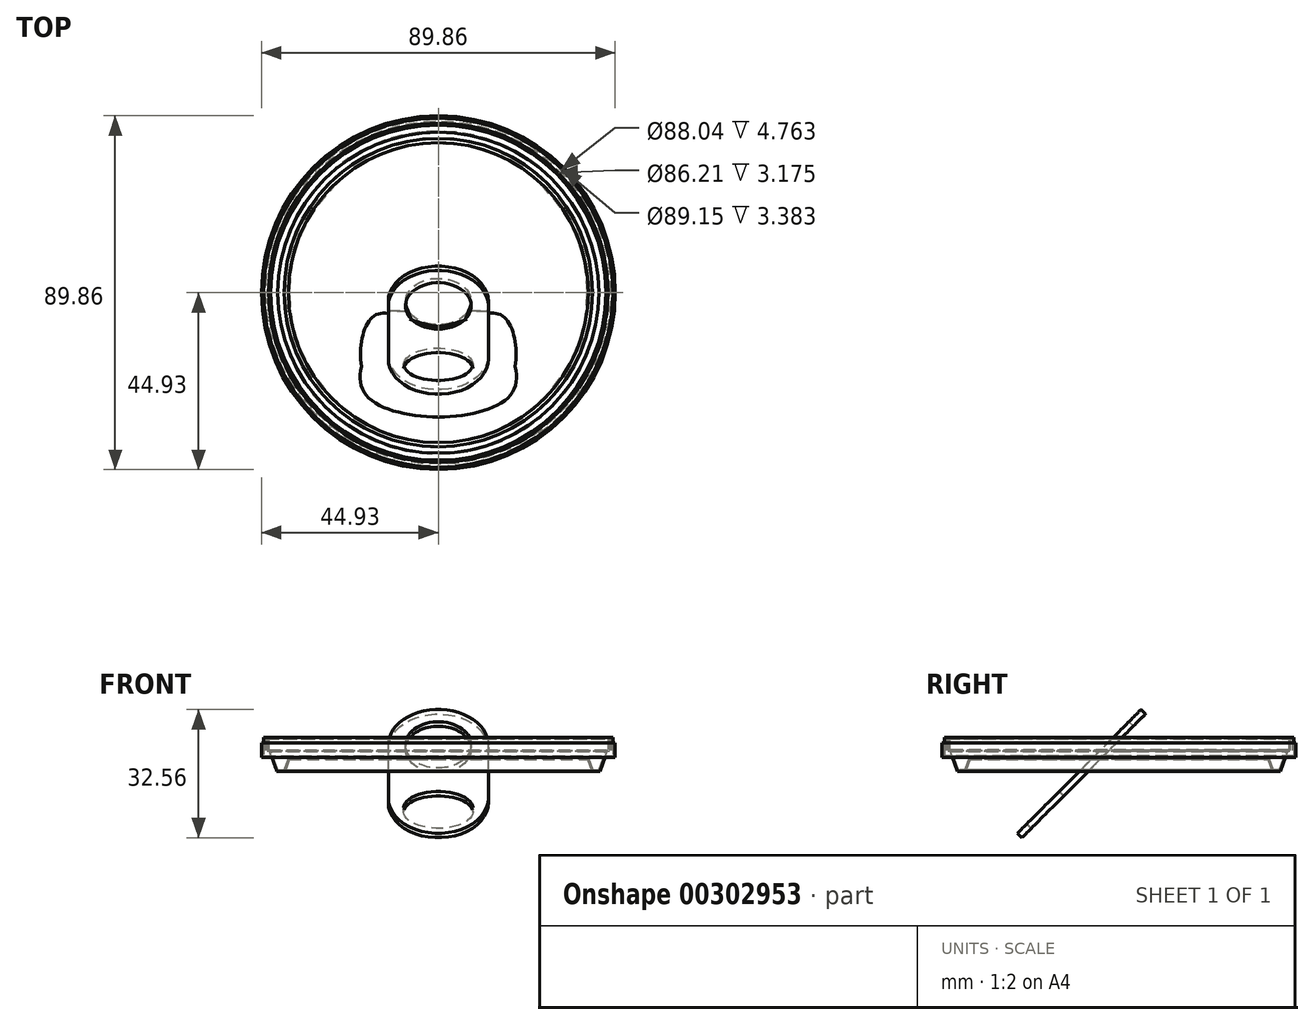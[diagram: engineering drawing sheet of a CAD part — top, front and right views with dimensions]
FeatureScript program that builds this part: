
annotation { "Feature Type Name" : "Feature", "Feature Type Description" : "" }
export const myFeature = defineFeature(function(context is Context, id is Id, definition is map)
    precondition{}
    {
        {
            var Q0;
            Q0=qCreatedBy(makeId("Front.planeOp"),FACE);
            var sketch = newSketch(context, id + "F0", { "sketchPlane" : qUnion([Q0])});
            skLineSegment(sketch, "E0", {"start": v(0, 0) * mm, "end": v(-38.1, 0) * mm});
            skLineSegment(sketch, "E1", {"start": v(-38.1, 0) * mm, "end": v(-39.19, -2.98) * mm});
            skLineSegment(sketch, "E2", {"start": v(-39.19, -2.98) * mm, "end": v(-40.77, -2.98) * mm});
            skLineSegment(sketch, "E3", {"start": v(-40.77, -2.98) * mm, "end": v(-42.57, 1.95) * mm});
            skLineSegment(sketch, "E4", {"start": v(-42.57, 1.95) * mm, "end": v(-43.1, 2.1) * mm});
            skLineSegment(sketch, "E5", {"start": v(-43.1, 2.1) * mm, "end": v(-43.1, 5.28) * mm});
            skLineSegment(sketch, "E6", {"start": v(-43.1, 5.28) * mm, "end": v(-44.37, 5.28) * mm});
            skLineSegment(sketch, "E7", {"start": v(-44.37, 5.28) * mm, "end": v(-44.37, 0.52) * mm});
            skLineSegment(sketch, "E8", {"start": v(-44.02, 0.16) * mm, "end": v(-44.02, 4.92) * mm});
            skLineSegment(sketch, "E9", {"start": v(-44.02, 4.92) * mm, "end": v(-43.46, 4.92) * mm});
            skLineSegment(sketch, "E10", {"start": v(-43.46, 4.92) * mm, "end": v(-43.46, 1.84) * mm});
            skLineSegment(sketch, "E11", {"start": v(-43.46, 1.84) * mm, "end": v(-42.84, 1.66) * mm});
            skLineSegment(sketch, "E12", {"start": v(-42.84, 1.66) * mm, "end": v(-41.02, -3.34) * mm});
            skLineSegment(sketch, "E13", {"start": v(-41.02, -3.34) * mm, "end": v(-38.94, -3.34) * mm});
            skLineSegment(sketch, "E14", {"start": v(-38.94, -3.34) * mm, "end": v(-37.85, -0.36) * mm});
            skLineSegment(sketch, "E15", {"start": v(-37.85, -0.36) * mm, "end": v(0, -0.36) * mm});
            skLineSegment(sketch, "E16", {"start": v(0, -0.36) * mm, "end": v(0, 0) * mm});
            skLineSegment(sketch, "E17", {"start": v(-44.37, 0.52) * mm, "end": v(-44.58, 0.52) * mm});
            skLineSegment(sketch, "E18", {"start": v(-44.58, 0.52) * mm, "end": v(-44.58, 3.9) * mm});
            skLineSegment(sketch, "E19", {"start": v(-44.58, 3.9) * mm, "end": v(-44.93, 3.9) * mm});
            skLineSegment(sketch, "E20", {"start": v(-44.93, 3.9) * mm, "end": v(-44.93, 0.16) * mm});
            skLineSegment(sketch, "E21", {"start": v(-44.93, 0.16) * mm, "end": v(-44.02, 0.16) * mm});
            skPoint(sketch, "E22.orphan", {"position": v(-41.58, 1.66) * mm});
            skSolve(sketch);
        }
        {
            var Q0;
            Q0=makeQuery(id+"F0.imprint","IMPRINT",FACE,{"disambiguationData":[TD([[makeQuery(id+"F0.imprint","IMPRINT",EDGE,{"derivedFrom":sQuery(id+"F0.wireOp",EDGE,"E0")}),1.0]])]});
            var Q1;
            Q1=sQuery(id+"F0.wireOp",EDGE,"E16");
            revolve(context, id + "F1", {"entities" : qUnion([Q0]), "axis" : qUnion([Q1]), "revolveType" : RevolveType.FULL});
        }
        {
            var Q0;
            Q0=makeQuery(id+"F1.opRevolve","SWEPT_FACE",FACE,{"disambiguationData":[OSD([sQuery(id+"F0.wireOp",EDGE,"E0")])]});
            var sketch = newSketch(context, id + "F2", { "sketchPlane" : qUnion([Q0])});
            skFitSpline(sketch, "E23", {"points": [v(0, -8.58) * mm, v(-11.44, -6.1) * mm, v(-18.01, -14.14) * mm, v(-18.7, -25.56) * mm, v(0, -31.59) * mm, v(18.18, -23.35) * mm, v(15.92, -5.7) * mm, v(0, -8.58) * mm]});
            skFitSpline(sketch, "E24.MirrorCS", {"points": [v(0, -8.58) * mm, v(11.44, -6.1) * mm, v(18.01, -14.14) * mm, v(18.7, -25.56) * mm, v(0, -31.59) * mm, v(-18.18, -23.35) * mm, v(-15.92, -5.7) * mm, v(0, -8.58) * mm]});
            skPoint(sketch, "E25.start.orphan", {"position": v(0, 14.42) * mm});
            skSolve(sketch);
        }
        {
            var Q0;
            Q0 = qSketchRegion(id + "F2", true);
            extrude(context, id + "F3", {"entities" : qUnion([Q0]), "operationType" : NewBodyOperationType.REMOVE, "oppositeDirection" : true, "depth" : 25.4 * mm});
        }
        {
            var Q0;
            Q0=qCreatedBy(makeId("Top.planeOp"),FACE);
            var Q1;
            Q1=sQuery(id+"F0.wireOp",EDGE,"E0");
            cPlane(context, id + "F4", {"entities" : qUnion([Q0, Q1]), "cplaneType" : CPlaneType.LINE_ANGLE, "offset" : 25.4 * mm, "angle" : 45 * degree, "oppositeDirection" : true, "width" : 152.4 * mm, "height" : 152.4 * mm});
        }
        {
            var Q0;
            Q0=qCreatedBy(id+"F4.planeOp",FACE);
            cPlane(context, id + "F5", {"entities" : qUnion([Q0]), "cplaneType" : CPlaneType.OFFSET, "offset" : 4.76 * mm, "oppositeDirection" : true, "width" : 152.4 * mm, "height" : 152.4 * mm});
        }
        {
            var Q0;
            Q0=qCreatedBy(id+"F5.planeOp",FACE);
            var sketch = newSketch(context, id + "F6", { "sketchPlane" : qUnion([Q0])});
            skLineSegment(sketch, "E26.bottom", {"start": v(0, -31.75) * mm, "end": v(0, -31.75) * mm});
            skLineSegment(sketch, "E26.top", {"start": v(0, 12.7) * mm, "end": v(0, 12.7) * mm});
            skLineSegment(sketch, "E26.left", {"start": v(-12.7, -19.05) * mm, "end": v(-12.7, 0) * mm});
            skLineSegment(sketch, "E26.right", {"start": v(12.7, -19.05) * mm, "end": v(12.7, 0) * mm});
            skPoint(sketch, "E27.visualSharp", {"position": v(-12.7, -31.75) * mm});
            skArc(sketch, "E27.filletArc", {"start": v(-12.7, -19.05) * mm, "mid": v(-8.98, -28.03) * mm, "end": v(0, -31.75) * mm});
            skPoint(sketch, "E28.visualSharp", {"position": v(12.7, -31.75) * mm});
            skArc(sketch, "E28.filletArc", {"start": v(0, -31.75) * mm, "mid": v(8.98, -28.03) * mm, "end": v(12.7, -19.05) * mm});
            skPoint(sketch, "E29.visualSharp", {"position": v(-12.7, 12.7) * mm});
            skArc(sketch, "E29.filletArc", {"start": v(0, 12.7) * mm, "mid": v(-8.98, 8.98) * mm, "end": v(-12.7, 0) * mm});
            skPoint(sketch, "E30.visualSharp", {"position": v(12.7, 12.7) * mm});
            skArc(sketch, "E30.filletArc", {"start": v(12.7, 0) * mm, "mid": v(8.98, 8.98) * mm, "end": v(0, 12.7) * mm});
            skCircle(sketch, "E31", {"center": v(0, 0) * mm, "radius": 8.33 * mm});
            skEllipse(sketch, "E32", {"center": v(0, -22.57) * mm, "majorRadius": 8.78 * mm, "minorRadius": 5.84 * mm, "majorAxis": v(1, 0)});
            skSolve(sketch);
        }
        {
            var Q0;
            Q0=makeQuery(id+"F6.imprint","IMPRINT",FACE,{"disambiguationData":[TD([[makeQuery(id+"F6.imprint","IMPRINT",EDGE,{"derivedFrom":sQuery(id+"F6.wireOp",EDGE,"E26.left")}),-1.0]])]});
            extrude(context, id + "F7", {"entities" : qUnion([Q0]), "operationType" : NewBodyOperationType.ADD, "depth" : 1.59 * mm});
        }
    });
